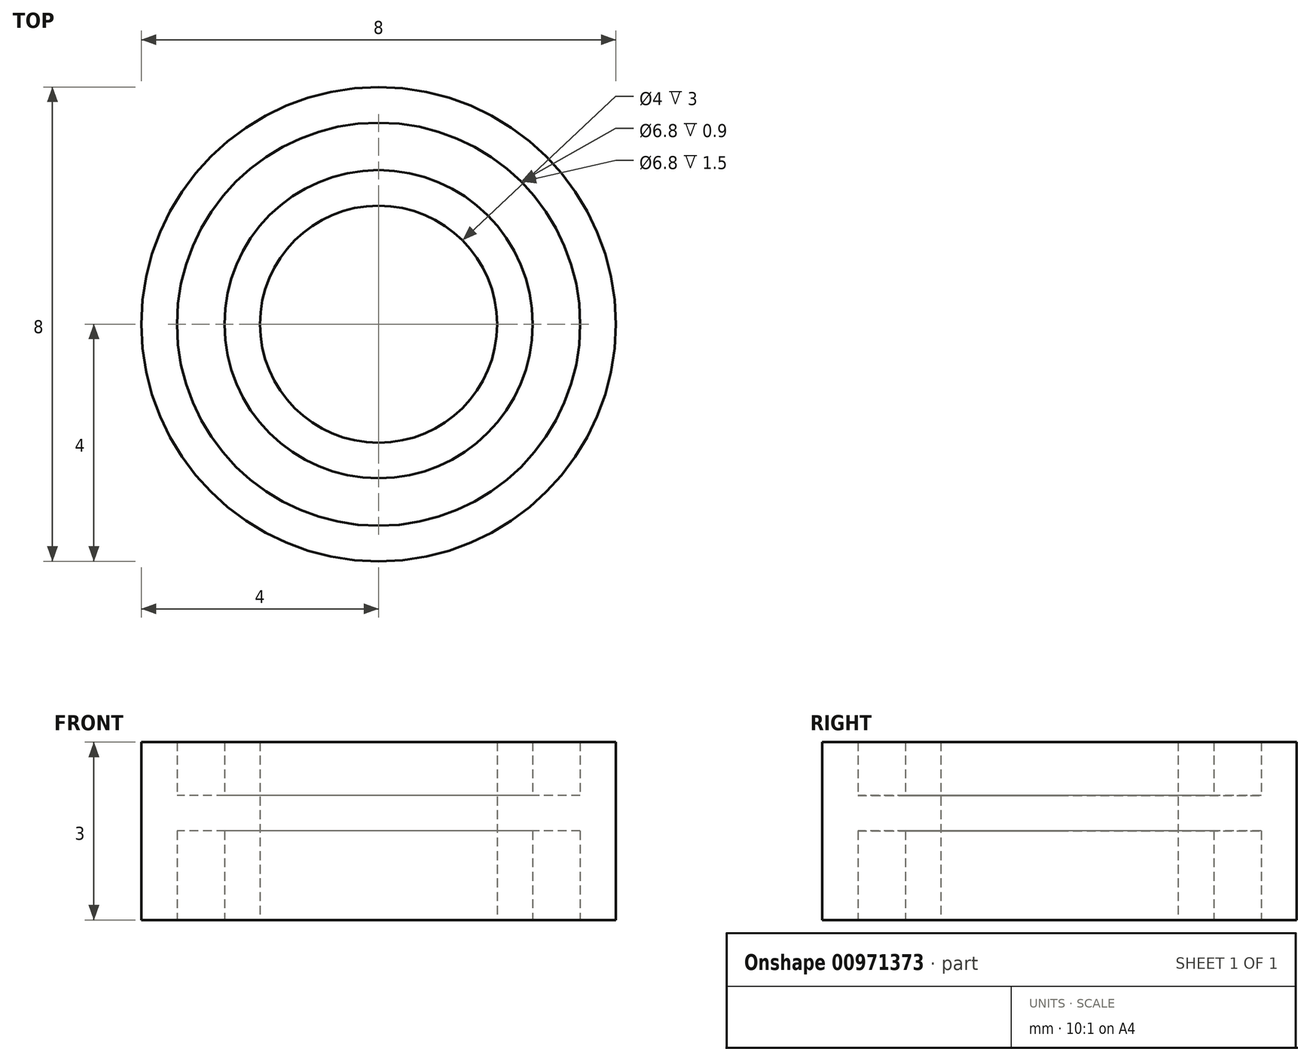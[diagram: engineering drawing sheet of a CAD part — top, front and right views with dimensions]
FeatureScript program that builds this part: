
annotation { "Feature Type Name" : "Feature", "Feature Type Description" : "" }
export const myFeature = defineFeature(function(context is Context, id is Id, definition is map)
    precondition{}
    {
        {
            var Q0;
            Q0=qCreatedBy(makeId("Top.planeOp"),FACE);
            var sketch = newSketch(context, id + "F0", { "sketchPlane" : qUnion([Q0])});
            skCircle(sketch, "E0", {"center": v(0, 0) * mm, "radius": 4 * mm});
            skCircle(sketch, "E1", {"center": v(0, 0) * mm, "radius": 2 * mm});
            skSolve(sketch);
        }
        {
            var Q0;
            Q0=makeQuery(id+"F0.imprint","IMPRINT",FACE,{"disambiguationData":[TD([[makeQuery(id+"F0.imprint","IMPRINT",EDGE,{"derivedFrom":sQuery(id+"F0.wireOp",EDGE,"E0")}),1.0]])]});
            extrude(context, id + "F1", {"entities" : qUnion([Q0]), "depth" : 1.5 * mm, "offsetDistance" : 25 * mm});
        }
        {
            var Q0;
            Q0=makeQuery(id+"F1.opExtrude","CAP_FACE",FACE,{"disambiguationData":[OSD([sQuery(id+"F0.wireOp",EDGE,"E0"),sQuery(id+"F0.wireOp",EDGE,"E1")])],"isStart":false});
            shell(context, id + "F2", {"entities" : qUnion([Q0]), "thickness" : .6 * mm});
        }
        {
            var Q0;
            Q0=makeQuery(id+"F1.opExtrude","CAP_FACE",FACE,{"disambiguationData":[OSD([sQuery(id+"F0.wireOp",EDGE,"E0"),sQuery(id+"F0.wireOp",EDGE,"E1")])],"isStart":true});
            extrude(context, id + "F3", {"entities" : qUnion([Q0]), "operationType" : NewBodyOperationType.ADD, "depth" : 1.5 * mm, "offsetDistance" : 25 * mm});
        }
        {
            var Q0;
            Q0=makeQuery(id+"F3.opExtrude","CAP_FACE",FACE,{"disambiguationData":[OSD([sQuery(id+"F0.wireOp",EDGE,"E0"),sQuery(id+"F0.wireOp",EDGE,"E1")])],"isStart":false});
            shell(context, id + "F4", {"entities" : qUnion([Q0]), "thickness" : .6 * mm});
        }
    });
